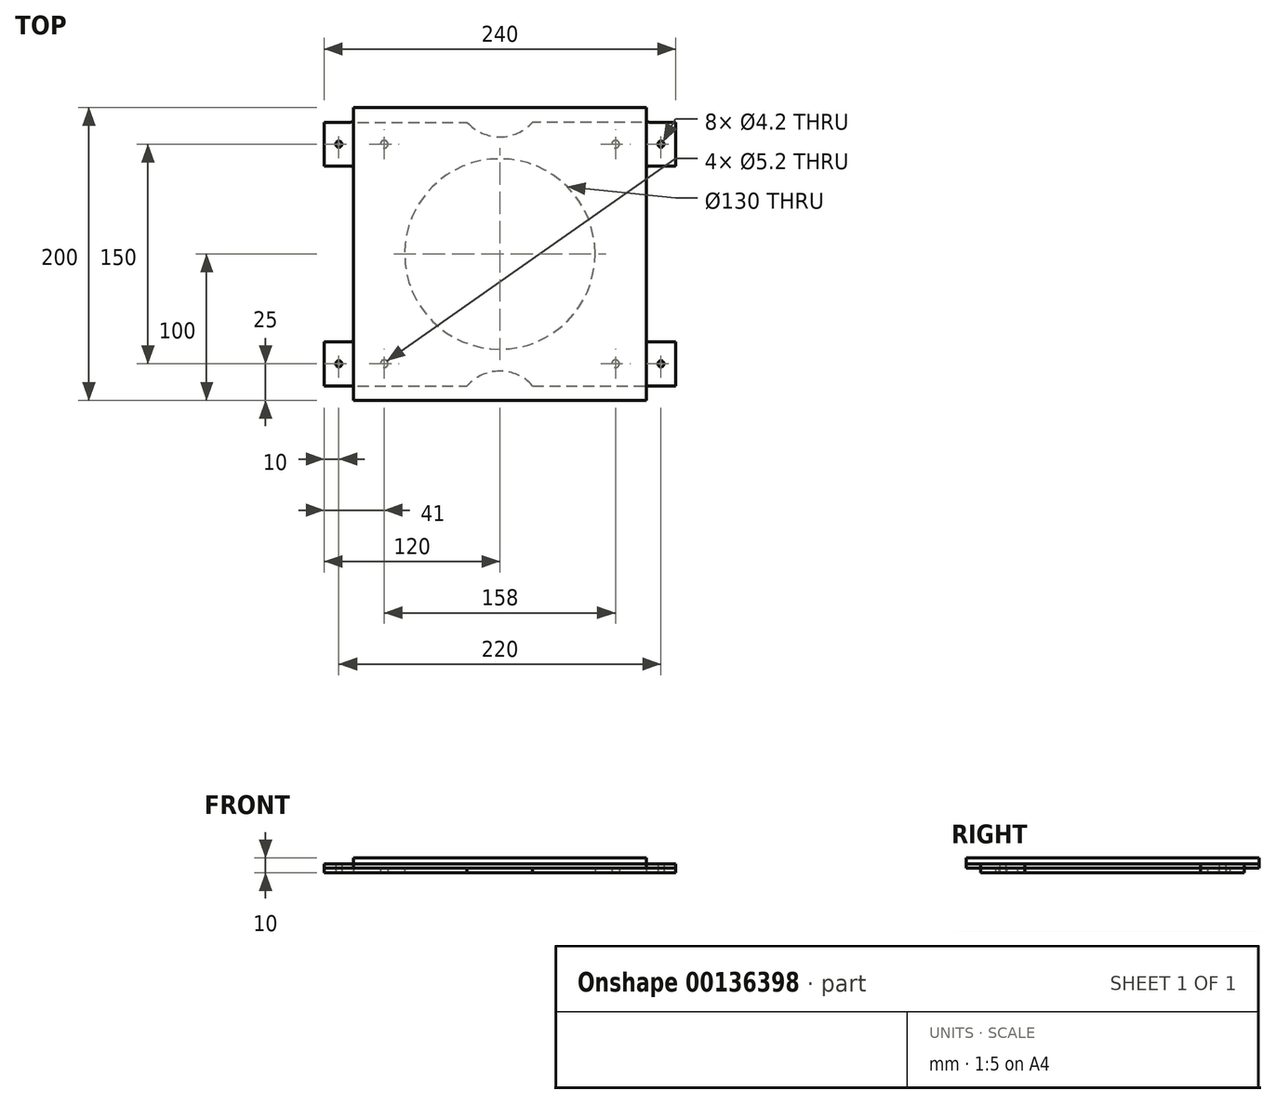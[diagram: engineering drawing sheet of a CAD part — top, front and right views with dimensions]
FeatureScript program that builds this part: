
annotation { "Feature Type Name" : "Feature", "Feature Type Description" : "" }
export const myFeature = defineFeature(function(context is Context, id is Id, definition is map)
    precondition{}
    {
        {
            var Q0;
            Q0=qCreatedBy(makeId("Top.planeOp"),FACE);
            var sketch = newSketch(context, id + "F0", { "sketchPlane" : qUnion([Q0])});
            skLineSegment(sketch, "E0.left", {"start": v(-120, -90) * mm, "end": v(-120, -60) * mm});
            skLineSegment(sketch, "E0.right", {"start": v(120, -90) * mm, "end": v(120, -60) * mm});
            skCircle(sketch, "E1", {"center": v(-79, 75) * mm, "radius": 2.6 * mm});
            skCircle(sketch, "E2", {"center": v(79, 75) * mm, "radius": 2.6 * mm});
            skCircle(sketch, "E3", {"center": v(79, -75) * mm, "radius": 2.6 * mm});
            skCircle(sketch, "E4", {"center": v(-79, -75) * mm, "radius": 2.6 * mm});
            skCircle(sketch, "E5", {"center": v(0, 0) * mm, "radius": 65 * mm});
            skArc(sketch, "E6", {"start": v(22.36, -90) * mm, "mid": v(0, -80) * mm, "end": v(-22.36, -90) * mm});
            skArc(sketch, "E7", {"start": v(-22.36, 90) * mm, "mid": v(0, 80) * mm, "end": v(22.36, 90) * mm});
            skLineSegment(sketch, "E8.bottom", {"start": v(-120, 90) * mm, "end": v(-102, 90) * mm});
            skLineSegment(sketch, "E8.top", {"start": v(-120, 60) * mm, "end": v(-102, 60) * mm});
            skLineSegment(sketch, "E8.left", {"start": v(-120, 90) * mm, "end": v(-120, 60) * mm});
            skLineSegment(sketch, "E9.bottom", {"start": v(-120, -60) * mm, "end": v(-102, -60) * mm});
            skLineSegment(sketch, "E9.top", {"start": v(-120, -90) * mm, "end": v(-102, -90) * mm});
            skLineSegment(sketch, "E9.left", {"start": v(-120, -60) * mm, "end": v(-120, -90) * mm});
            skLineSegment(sketch, "E10.trimOffspring", {"start": v(-120, 60) * mm, "end": v(-120, 90) * mm});
            skLineSegment(sketch, "E11.trimOffspring", {"start": v(-100, 58) * mm, "end": v(-100, -58) * mm});
            skLineSegment(sketch, "E12.MirrorCS", {"start": v(120, -60) * mm, "end": v(120, -90) * mm});
            skLineSegment(sketch, "E13.MirrorCS", {"start": v(120, -90) * mm, "end": v(102, -90) * mm});
            skLineSegment(sketch, "E14.MirrorCS", {"start": v(120, -60) * mm, "end": v(102, -60) * mm});
            skLineSegment(sketch, "E15.MirrorCS", {"start": v(120, 60) * mm, "end": v(102, 60) * mm});
            skLineSegment(sketch, "E16.MirrorCS", {"start": v(120, 90) * mm, "end": v(102, 90) * mm});
            skLineSegment(sketch, "E17.MirrorCS", {"start": v(120, 60) * mm, "end": v(120, 90) * mm});
            skLineSegment(sketch, "E18.trimOffspring", {"start": v(100, 58) * mm, "end": v(100, -58) * mm});
            skPoint(sketch, "E19.visualSharp", {"position": v(-100, 60) * mm});
            skArc(sketch, "E19.filletArc", {"start": v(-100, 58) * mm, "mid": v(-100.59, 59.41) * mm, "end": v(-102, 60) * mm});
            skPoint(sketch, "E20.visualSharp", {"position": v(-100, -60) * mm});
            skArc(sketch, "E20.filletArc", {"start": v(-102, -60) * mm, "mid": v(-100.59, -59.41) * mm, "end": v(-100, -58) * mm});
            skPoint(sketch, "E21.visualSharp", {"position": v(100, -60) * mm});
            skArc(sketch, "E21.filletArc", {"start": v(100, -58) * mm, "mid": v(100.59, -59.41) * mm, "end": v(102, -60) * mm});
            skPoint(sketch, "E22.visualSharp", {"position": v(100, 60) * mm});
            skArc(sketch, "E22.filletArc", {"start": v(102, 60) * mm, "mid": v(100.59, 59.41) * mm, "end": v(100, 58) * mm});
            skPoint(sketch, "E23.visualSharp", {"position": v(100, 90) * mm});
            skCircle(sketch, "E24", {"center": v(-110, 75) * mm, "radius": 2.1 * mm});
            skCircle(sketch, "E25", {"center": v(-110, -75) * mm, "radius": 2.1 * mm});
            skCircle(sketch, "E26.MirrorC", {"center": v(110, 75) * mm, "radius": 2.1 * mm});
            skCircle(sketch, "E27.MirrorC", {"center": v(110, -75) * mm, "radius": 2.1 * mm});
            skLineSegment(sketch, "E28", {"start": v(-102, -90) * mm, "end": v(102, -90) * mm});
            skLineSegment(sketch, "E29", {"start": v(-102, 90) * mm, "end": v(102, 90) * mm});
            skSolve(sketch);
        }
        {
            var Q0;
            Q0=makeQuery(id+"F0.imprint","IMPRINT",FACE,{"disambiguationData":[TD([[makeQuery(id+"F0.imprint","IMPRINT",EDGE,{"derivedFrom":sQuery(id+"F0.wireOp",EDGE,"E1")}),-1.0]])]});
            extrude(context, id + "F1", {"entities" : qUnion([Q0]), "depth" : 3 * mm});
        }
        {
            var Q0;
            Q0=makeQuery(id+"F1.opExtrude","CAP_FACE",FACE,{"disambiguationData":[OSD([sQuery(id+"F0.wireOp",EDGE,"E0.bottom"),sQuery(id+"F0.wireOp",EDGE,"E0.top"),sQuery(id+"F0.wireOp",EDGE,"E1"),sQuery(id+"F0.wireOp",EDGE,"E2"),sQuery(id+"F0.wireOp",EDGE,"E3"),sQuery(id+"F0.wireOp",EDGE,"E4"),sQuery(id+"F0.wireOp",EDGE,"E5"),sQuery(id+"F0.wireOp",EDGE,"E6"),sQuery(id+"F0.wireOp",EDGE,"E7"),sQuery(id+"F0.wireOp",EDGE,"E8.bottom"),sQuery(id+"F0.wireOp",EDGE,"E8.top"),sQuery(id+"F0.wireOp",EDGE,"E9.bottom"),sQuery(id+"F0.wireOp",EDGE,"E9.top"),sQuery(id+"F0.wireOp",EDGE,"E9.left"),sQuery(id+"F0.wireOp",EDGE,"BvpuSFxZ-txSK-8JEX-lZ7i-zpK9JLGWmF4Y"),sQuery(id+"F0.wireOp",EDGE,"E10.trimOffspring"),sQuery(id+"F0.wireOp",EDGE,"ZhbIfy4v-T8e5-uchx-f2dT-a7q0jufO3Gai"),sQuery(id+"F0.wireOp",EDGE,"d8c2181a-16b2-4424-900c-a954937d3f67.trimOffspring"),sQuery(id+"F0.wireOp",EDGE,"E11.trimOffspring"),sQuery(id+"F0.wireOp",EDGE,"E12.MirrorCS"),sQuery(id+"F0.wireOp",EDGE,"E13.MirrorCS"),sQuery(id+"F0.wireOp",EDGE,"E14.MirrorCS"),sQuery(id+"F0.wireOp",EDGE,"E15.MirrorCS"),sQuery(id+"F0.wireOp",EDGE,"E16.MirrorCS"),sQuery(id+"F0.wireOp",EDGE,"E18.trimOffspring"),sQuery(id+"F0.wireOp",EDGE,"E17.MirrorCS"),sQuery(id+"F0.wireOp",EDGE,"83ceebcb-7b96-4a8d-9a07-ca30cf589b91.trimOffspring"),sQuery(id+"F0.wireOp",EDGE,"1aa5cba0-18d4-4be6-8098-e044005c8ec5.trimOffspring"),sQuery(id+"F0.wireOp",EDGE,"9e6ad601-b2ff-4236-bbc8-cf0d715f3197.trimOffspring"),sQuery(id+"F0.wireOp",EDGE,"370b523b-0918-4bff-a78e-4fa7f3aa4643.filletArc"),sQuery(id+"F0.wireOp",EDGE,"38a18e43-722f-4787-af12-905f5473f790.filletArc"),sQuery(id+"F0.wireOp",EDGE,"06c33557-bd64-4ce1-99f8-836d622c79e1.filletArc"),sQuery(id+"F0.wireOp",EDGE,"1c6ff79e-df61-44f2-897d-d68faef84e5a.filletArc"),sQuery(id+"F0.wireOp",EDGE,"98c42b75-4196-4b9d-a52a-fab940d31304.filletArc"),sQuery(id+"F0.wireOp",EDGE,"E19.filletArc"),sQuery(id+"F0.wireOp",EDGE,"E20.filletArc"),sQuery(id+"F0.wireOp",EDGE,"b07fb7e1-fde7-4e9d-9fb8-860fe7d0986d.filletArc"),sQuery(id+"F0.wireOp",EDGE,"eebf30c6-8e33-4b0d-871f-d7e5c517970d.filletArc"),sQuery(id+"F0.wireOp",EDGE,"25a81ee7-2ad1-44f6-9dd4-ed7dcdd4ea3a.filletArc"),sQuery(id+"F0.wireOp",EDGE,"d8148b86-e109-44b7-9a36-9bc41ce57a51.filletArc"),sQuery(id+"F0.wireOp",EDGE,"E21.filletArc"),sQuery(id+"F0.wireOp",EDGE,"E22.filletArc"),sQuery(id+"F0.wireOp",EDGE,"E23.filletArc"),sQuery(id+"F0.wireOp",EDGE,"12e8851f-7d54-4070-bbab-77f286f93412.filletArc"),sQuery(id+"F0.wireOp",EDGE,"3cade0fd-60d8-4fd1-8e78-503ea9ea390b.filletArc"),sQuery(id+"F0.wireOp",EDGE,"E24"),sQuery(id+"F0.wireOp",EDGE,"E25"),sQuery(id+"F0.wireOp",EDGE,"E26.MirrorC"),sQuery(id+"F0.wireOp",EDGE,"E27.MirrorC")])],"isStart":false});
            var sketch = newSketch(context, id + "F2", { "sketchPlane" : qUnion([Q0])});
            skLineSegment(sketch, "E30.bottom", {"start": v(-100, 100) * mm, "end": v(100, 100) * mm});
            skLineSegment(sketch, "E30.top", {"start": v(-100, -100) * mm, "end": v(100, -100) * mm});
            skLineSegment(sketch, "E30.left", {"start": v(-100, 100) * mm, "end": v(-100, 92) * mm});
            skLineSegment(sketch, "E30.right", {"start": v(100, 100) * mm, "end": v(100, 92) * mm});
            skLineSegment(sketch, "E31.bottom", {"start": v(120, 90) * mm, "end": v(102, 90) * mm});
            skLineSegment(sketch, "E31.top", {"start": v(120, 60) * mm, "end": v(102, 60) * mm});
            skLineSegment(sketch, "E31.left", {"start": v(120, 90) * mm, "end": v(120, 60) * mm});
            skLineSegment(sketch, "E32.bottom", {"start": v(120, -60) * mm, "end": v(102, -60) * mm});
            skLineSegment(sketch, "E32.top", {"start": v(120, -90) * mm, "end": v(102, -90) * mm});
            skLineSegment(sketch, "E32.left", {"start": v(120, -60) * mm, "end": v(120, -90) * mm});
            skLineSegment(sketch, "E33.trimOffspring", {"start": v(100, 58) * mm, "end": v(100, -58) * mm});
            skLineSegment(sketch, "E34.trimOffspring", {"start": v(100, -92) * mm, "end": v(100, -100) * mm});
            skPoint(sketch, "E35.visualSharp", {"position": v(100, 90) * mm});
            skArc(sketch, "E35.filletArc", {"start": v(100, 92) * mm, "mid": v(100.59, 90.59) * mm, "end": v(102, 90) * mm});
            skPoint(sketch, "E36.visualSharp", {"position": v(100, 60) * mm});
            skArc(sketch, "E36.filletArc", {"start": v(102, 60) * mm, "mid": v(100.59, 59.41) * mm, "end": v(100, 58) * mm});
            skPoint(sketch, "E37.visualSharp", {"position": v(100, -60) * mm});
            skArc(sketch, "E37.filletArc", {"start": v(100, -58) * mm, "mid": v(100.59, -59.41) * mm, "end": v(102, -60) * mm});
            skPoint(sketch, "E38.visualSharp", {"position": v(100, -90) * mm});
            skArc(sketch, "E38.filletArc", {"start": v(102, -90) * mm, "mid": v(100.59, -90.59) * mm, "end": v(100, -92) * mm});
            skArc(sketch, "E39.MirrorCS", {"start": v(-100, 92) * mm, "mid": v(-100.59, 90.59) * mm, "end": v(-102, 90) * mm});
            skLineSegment(sketch, "E40.MirrorCS", {"start": v(-120, 90) * mm, "end": v(-102, 90) * mm});
            skLineSegment(sketch, "E41.MirrorCS", {"start": v(-120, 90) * mm, "end": v(-120, 60) * mm});
            skArc(sketch, "E42.MirrorCS", {"start": v(-102, 60) * mm, "mid": v(-100.59, 59.41) * mm, "end": v(-100, 58) * mm});
            skLineSegment(sketch, "E43.MirrorCS", {"start": v(-120, 60) * mm, "end": v(-102, 60) * mm});
            skArc(sketch, "E44.MirrorCS", {"start": v(-102, -90) * mm, "mid": v(-100.59, -90.59) * mm, "end": v(-100, -92) * mm});
            skLineSegment(sketch, "E45.MirrorCS", {"start": v(-120, -90) * mm, "end": v(-102, -90) * mm});
            skLineSegment(sketch, "E46.MirrorCS", {"start": v(-120, -60) * mm, "end": v(-102, -60) * mm});
            skLineSegment(sketch, "E47.MirrorCS", {"start": v(-120, -60) * mm, "end": v(-120, -90) * mm});
            skLineSegment(sketch, "E48.trimOffspring", {"start": v(-100, -92) * mm, "end": v(-100, -100) * mm});
            skSolve(sketch);
        }
        {
            var Q0;
            {var subQ1=sQuery(id+"F2.wireOp",EDGE,"E31.bottom");Q0=makeQuery(id+"F2.imprint","IMPRINT",FACE,{"disambiguationData":[TD([[makeQuery(id+"F2.imprint","IMPRINT",EDGE,{"derivedFrom":subQ1}),1.0]])]});}
            var Q1;
            Q1=makeQuery(id+"F2.imprint","IMPRINT",FACE,{"disambiguationData":[TD([[makeQuery(id+"F2.imprint","IMPRINT",EDGE,{"derivedFrom":sQuery(id+"F2.wireOp",EDGE,"E30.bottom")}),-1.0]])]});
            var Q2;
            Q2=makeQuery(id+"F2.imprint","IMPRINT",FACE,{"disambiguationData":[TD([[makeQuery(id+"F2.imprint","IMPRINT",EDGE,{"derivedFrom":makeQuery(id+"F1.opExtrude","CAP_EDGE",EDGE,{"disambiguationData":[OSD([sQuery(id+"F0.wireOp",EDGE,"E1")])],"isStart":false})}),1.0]])]});
            var Q3;
            Q3=makeQuery(id+"F2.imprint","IMPRINT",FACE,{"disambiguationData":[TD([[makeQuery(id+"F2.imprint","IMPRINT",EDGE,{"derivedFrom":makeQuery(id+"F1.opExtrude","CAP_EDGE",EDGE,{"disambiguationData":[OSD([sQuery(id+"F0.wireOp",EDGE,"E5")])],"isStart":false})}),1.0]])]});
            var Q4;
            Q4=makeQuery(id+"F2.imprint","IMPRINT",FACE,{"disambiguationData":[TD([[makeQuery(id+"F2.imprint","IMPRINT",EDGE,{"derivedFrom":makeQuery(id+"F1.opExtrude","CAP_EDGE",EDGE,{"disambiguationData":[OSD([sQuery(id+"F0.wireOp",EDGE,"E2")])],"isStart":false})}),1.0]])]});
            var Q5;
            Q5=makeQuery(id+"F2.imprint","IMPRINT",FACE,{"disambiguationData":[TD([[makeQuery(id+"F2.imprint","IMPRINT",EDGE,{"derivedFrom":makeQuery(id+"F1.opExtrude","CAP_EDGE",EDGE,{"disambiguationData":[OSD([sQuery(id+"F0.wireOp",EDGE,"E3")])],"isStart":false})}),1.0]])]});
            var Q6;
            Q6=makeQuery(id+"F2.imprint","IMPRINT",FACE,{"disambiguationData":[TD([[makeQuery(id+"F2.imprint","IMPRINT",EDGE,{"derivedFrom":sQuery(id+"F2.wireOp",EDGE,"E30.top")}),1.0]])]});
            var Q7;
            Q7=makeQuery(id+"F2.imprint","IMPRINT",FACE,{"disambiguationData":[TD([[makeQuery(id+"F2.imprint","IMPRINT",EDGE,{"derivedFrom":makeQuery(id+"F1.opExtrude","CAP_EDGE",EDGE,{"disambiguationData":[OSD([sQuery(id+"F0.wireOp",EDGE,"E4")])],"isStart":false})}),1.0]])]});
            extrude(context, id + "F3", {"entities" : qUnion([Q0, Q1, Q2, Q3, Q4, Q5, Q6, Q7]), "depth" : 3 * mm});
        }
        {
            var Q0;
            Q0=makeQuery(id+"F3.opExtrude","CAP_FACE",FACE,{"disambiguationData":[OSD([sQuery(id+"F0.wireOp",EDGE,"E11.trimOffspring"),sQuery(id+"F0.wireOp",EDGE,"E20.filletArc"),sQuery(id+"F0.wireOp",EDGE,"E24"),sQuery(id+"F0.wireOp",EDGE,"E25"),sQuery(id+"F0.wireOp",EDGE,"E26.MirrorC"),sQuery(id+"F0.wireOp",EDGE,"E27.MirrorC"),sQuery(id+"F2.wireOp",EDGE,"E30.bottom"),sQuery(id+"F2.wireOp",EDGE,"E30.top"),sQuery(id+"F2.wireOp",EDGE,"E30.left"),sQuery(id+"F2.wireOp",EDGE,"E30.right"),sQuery(id+"F2.wireOp",EDGE,"E31.bottom"),sQuery(id+"F2.wireOp",EDGE,"E31.top"),sQuery(id+"F2.wireOp",EDGE,"E31.left"),sQuery(id+"F2.wireOp",EDGE,"E32.bottom"),sQuery(id+"F2.wireOp",EDGE,"E32.top"),sQuery(id+"F2.wireOp",EDGE,"E32.left"),sQuery(id+"F2.wireOp",EDGE,"E33.trimOffspring"),sQuery(id+"F2.wireOp",EDGE,"E34.trimOffspring"),sQuery(id+"F2.wireOp",EDGE,"E35.filletArc"),sQuery(id+"F2.wireOp",EDGE,"E36.filletArc"),sQuery(id+"F2.wireOp",EDGE,"E37.filletArc"),sQuery(id+"F2.wireOp",EDGE,"E38.filletArc"),sQuery(id+"F2.wireOp",EDGE,"E39.MirrorCS"),sQuery(id+"F2.wireOp",EDGE,"E40.MirrorCS"),sQuery(id+"F2.wireOp",EDGE,"E41.MirrorCS"),sQuery(id+"F2.wireOp",EDGE,"E42.MirrorCS"),sQuery(id+"F2.wireOp",EDGE,"E43.MirrorCS"),sQuery(id+"F2.wireOp",EDGE,"E44.MirrorCS"),sQuery(id+"F2.wireOp",EDGE,"E45.MirrorCS"),sQuery(id+"F2.wireOp",EDGE,"E46.MirrorCS"),sQuery(id+"F2.wireOp",EDGE,"E47.MirrorCS"),sQuery(id+"F2.wireOp",EDGE,"E48.trimOffspring")])],"isStart":false});
            var sketch = newSketch(context, id + "F4", { "sketchPlane" : qUnion([Q0])});
            skLineSegment(sketch, "E49.bottom", {"start": v(-100, 100) * mm, "end": v(100, 100) * mm});
            skLineSegment(sketch, "E49.top", {"start": v(-100, -100) * mm, "end": v(100, -100) * mm});
            skLineSegment(sketch, "E49.left", {"start": v(-100, 100) * mm, "end": v(-100, -100) * mm});
            skLineSegment(sketch, "E49.right", {"start": v(100, 100) * mm, "end": v(100, -100) * mm});
            skSolve(sketch);
        }
        {
            var Q0;
            {var subQ2=sQuery(id+"F4.wireOp",EDGE,"E49.bottom");Q0=makeQuery(id+"F4.imprint","IMPRINT",FACE,{"disambiguationData":[TD([[makeQuery(id+"F4.imprint","IMPRINT",EDGE,{"derivedFrom":subQ2}),-1.0]])]});}
            var Q1;
            Q1=makeQuery(id+"F4.imprint","IMPRINT",FACE,{"disambiguationData":[TD([[makeQuery(id+"F4.imprint","IMPRINT",EDGE,{"derivedFrom":makeQuery(id+"F3.opExtrude","CAP_EDGE",EDGE,{"disambiguationData":[OSD([sQuery(id+"F0.wireOp",EDGE,"E1")])],"isStart":false})}),1.0]])]});
            var Q2;
            Q2=makeQuery(id+"F4.imprint","IMPRINT",FACE,{"disambiguationData":[TD([[makeQuery(id+"F4.imprint","IMPRINT",EDGE,{"derivedFrom":makeQuery(id+"F3.opExtrude","CAP_EDGE",EDGE,{"disambiguationData":[OSD([sQuery(id+"F0.wireOp",EDGE,"E4")])],"isStart":false})}),1.0]])]});
            var Q3;
            Q3=makeQuery(id+"F4.imprint","IMPRINT",FACE,{"disambiguationData":[TD([[makeQuery(id+"F4.imprint","IMPRINT",EDGE,{"derivedFrom":makeQuery(id+"F3.opExtrude","CAP_EDGE",EDGE,{"disambiguationData":[OSD([sQuery(id+"F0.wireOp",EDGE,"E3")])],"isStart":false})}),1.0]])]});
            var Q4;
            Q4=makeQuery(id+"F4.imprint","IMPRINT",FACE,{"disambiguationData":[TD([[makeQuery(id+"F4.imprint","IMPRINT",EDGE,{"derivedFrom":makeQuery(id+"F3.opExtrude","CAP_EDGE",EDGE,{"disambiguationData":[OSD([sQuery(id+"F0.wireOp",EDGE,"E2")])],"isStart":false})}),1.0]])]});
            extrude(context, id + "F5", {"entities" : qUnion([Q0, Q1, Q2, Q3, Q4]), "depth" : 4 * mm});
        }
    });
